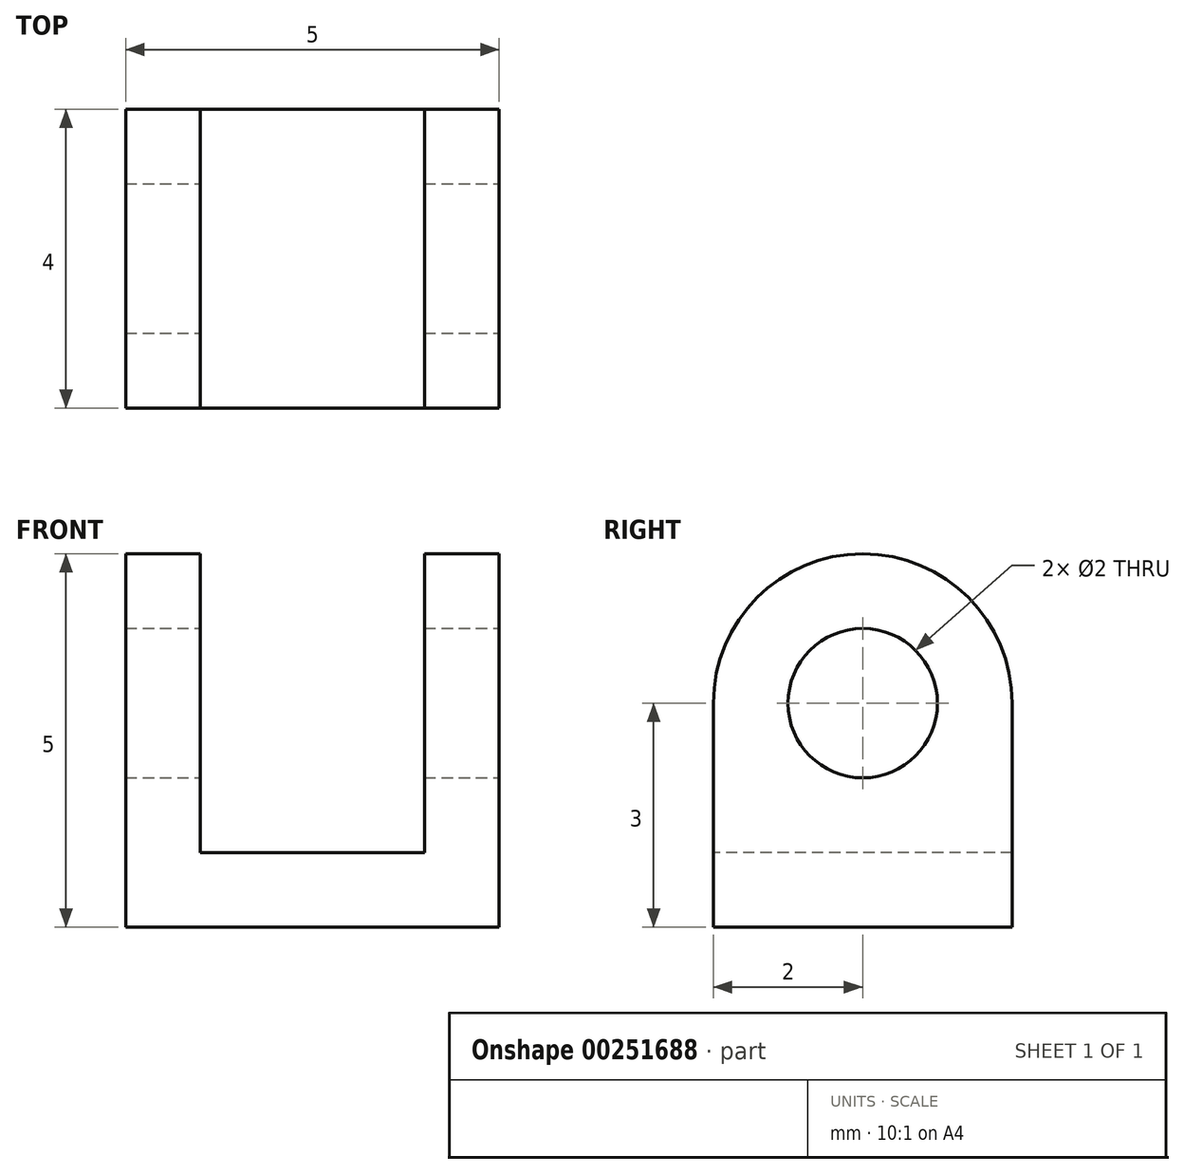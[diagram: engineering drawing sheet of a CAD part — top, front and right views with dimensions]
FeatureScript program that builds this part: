
annotation { "Feature Type Name" : "Feature", "Feature Type Description" : "" }
export const myFeature = defineFeature(function(context is Context, id is Id, definition is map)
    precondition{}
    {
        {
            var Q0;
            Q0=qCreatedBy(makeId("Top.planeOp"),FACE);
            var sketch = newSketch(context, id + "F0", { "sketchPlane" : qUnion([Q0])});
            skLineSegment(sketch, "E0.bottom", {"start": v(0, 0) * mm, "end": v(5, 0) * mm});
            skLineSegment(sketch, "E0.top", {"start": v(0, 4) * mm, "end": v(5, 4) * mm});
            skLineSegment(sketch, "E0.left", {"start": v(0, 0) * mm, "end": v(0, 4) * mm});
            skLineSegment(sketch, "E0.right", {"start": v(5, 0) * mm, "end": v(5, 4) * mm});
            skSolve(sketch);
        }
        {
            var Q0;
            Q0 = qSketchRegion(id + "F0", true);
            extrude(context, id + "F1", {"entities" : qUnion([Q0]), "depth" : 5 * mm});
        }
        {
            var Q0;
            Q0=makeQuery(id+"F1.opExtrude","CAP_EDGE",EDGE,{"disambiguationData":[OSD([sQuery(id+"F0.wireOp",EDGE,"E0.bottom")])],"isStart":false});
            var Q1;
            Q1=makeQuery(id+"F1.opExtrude","CAP_EDGE",EDGE,{"disambiguationData":[OSD([sQuery(id+"F0.wireOp",EDGE,"E0.top")])],"isStart":false});
            fillet(context, id + "F2", {"entities" : qUnion([Q0, Q1]), "radius" : 2 * mm, "tangentPropagation" : true, "allowEdgeOverflow" : false});
        }
        {
            var Q0;
            Q0=makeQuery(id+"F1.opExtrude","SWEPT_FACE",FACE,{"disambiguationData":[OSD([sQuery(id+"F0.wireOp",EDGE,"E0.right")])]});
            var sketch = newSketch(context, id + "F3", { "sketchPlane" : qUnion([Q0])});
            skLineSegment(sketch, "E1", {"start": v(2, 5) * mm, "end": v(2, 3) * mm, "construction": true});
            skPoint(sketch, "E1.endSnap0", {"position": v(2, 5) * mm});
            skCircle(sketch, "E2", {"center": v(2, 3) * mm, "radius": 1 * mm});
            skSolve(sketch);
        }
        {
            var Q0;
            Q0 = qSketchRegion(id + "F3", true);
            extrude(context, id + "F4", {"entities" : qUnion([Q0]), "operationType" : NewBodyOperationType.REMOVE, "oppositeDirection" : true, "depth" : 25 * mm});
        }
        {
            var Q0;
            {var subQ0=sQuery(id+"F0.wireOp",EDGE,"E0.top");Q0=makeQuery(id+"F2.opFillet","BLEND_VERTEX",VERTEX,{"blendedFrom":[makeQuery(id+"F1.opExtrude","CAP_EDGE",EDGE,{"disambiguationData":[OSD([subQ0])],"isStart":false}),makeQuery(id+"F1.opExtrude","SWEPT_FACE",FACE,{"disambiguationData":[OSD([subQ0])]}),makeQuery(id+"F1.opExtrude","SWEPT_FACE",FACE,{"disambiguationData":[OSD([sQuery(id+"F0.wireOp",EDGE,"E0.left")])]})],"blendedInto":[makeQuery(id+"F1.opExtrude","SWEPT_FACE",FACE,{"disambiguationData":[OSD([subQ0])]}),makeQuery(id+"F1.opExtrude","SWEPT_FACE",FACE,{"disambiguationData":[OSD([sQuery(id+"F0.wireOp",EDGE,"E0.left")])]})]});}
            var Q1;
            {var subQ0=sQuery(id+"F0.wireOp",EDGE,"E0.top");Q1=makeQuery(id+"F2.opFillet","BLEND_VERTEX",VERTEX,{"blendedFrom":[makeQuery(id+"F1.opExtrude","CAP_EDGE",EDGE,{"disambiguationData":[OSD([subQ0])],"isStart":false}),makeQuery(id+"F1.opExtrude","SWEPT_FACE",FACE,{"disambiguationData":[OSD([subQ0])]}),makeQuery(id+"F1.opExtrude","SWEPT_FACE",FACE,{"disambiguationData":[OSD([sQuery(id+"F0.wireOp",EDGE,"E0.right")])]})],"blendedInto":[makeQuery(id+"F1.opExtrude","SWEPT_FACE",FACE,{"disambiguationData":[OSD([subQ0])]}),makeQuery(id+"F1.opExtrude","SWEPT_FACE",FACE,{"disambiguationData":[OSD([sQuery(id+"F0.wireOp",EDGE,"E0.right")])]})]});}
            var Q2;
            {var subQ0=sQuery(id+"F0.wireOp",EDGE,"E0.bottom");Q2=makeQuery(id+"F2.opFillet","BLEND_VERTEX",VERTEX,{"blendedFrom":[makeQuery(id+"F1.opExtrude","CAP_EDGE",EDGE,{"disambiguationData":[OSD([subQ0])],"isStart":false}),makeQuery(id+"F1.opExtrude","SWEPT_FACE",FACE,{"disambiguationData":[OSD([subQ0])]}),makeQuery(id+"F1.opExtrude","SWEPT_FACE",FACE,{"disambiguationData":[OSD([sQuery(id+"F0.wireOp",EDGE,"E0.left")])]})],"blendedInto":[makeQuery(id+"F1.opExtrude","SWEPT_FACE",FACE,{"disambiguationData":[OSD([subQ0])]}),makeQuery(id+"F1.opExtrude","SWEPT_FACE",FACE,{"disambiguationData":[OSD([sQuery(id+"F0.wireOp",EDGE,"E0.left")])]})]});}
            cPlane(context, id + "F5", {"entities" : qUnion([Q0, Q1, Q2]), "cplaneType" : CPlaneType.THREE_POINT, "offset" : 25 * mm, "width" : 150 * mm, "height" : 150 * mm});
        }
        {
            var Q0;
            Q0=qCreatedBy(id+"F5.planeOp",FACE);
            cPlane(context, id + "F6", {"entities" : qUnion([Q0]), "cplaneType" : CPlaneType.OFFSET, "offset" : 2 * mm, "width" : 150 * mm, "height" : 150 * mm});
        }
        {
            var Q0;
            Q0=qCreatedBy(id+"F6.planeOp",FACE);
            var sketch = newSketch(context, id + "F7", { "sketchPlane" : qUnion([Q0])});
            skPoint(sketch, "E3.0", {"position": v(0, 4) * mm});
            skPoint(sketch, "E3.1", {"position": v(5, 4) * mm});
            skPoint(sketch, "E3.2", {"position": v(5, 0) * mm});
            skPoint(sketch, "E3.3", {"position": v(0, 0) * mm});
            skLineSegment(sketch, "E4", {"start": v(0, 4) * mm, "end": v(1, 4) * mm, "construction": true});
            skLineSegment(sketch, "E5", {"start": v(1, 4) * mm, "end": v(1, 0) * mm});
            skLineSegment(sketch, "E6", {"start": v(5, 4) * mm, "end": v(4, 4) * mm, "construction": true});
            skLineSegment(sketch, "E7", {"start": v(4, 4) * mm, "end": v(4, 0) * mm});
            skLineSegment(sketch, "E8", {"start": v(1, 0) * mm, "end": v(4, 0) * mm});
            skLineSegment(sketch, "E9", {"start": v(4, 4) * mm, "end": v(1, 4) * mm});
            skSolve(sketch);
        }
        {
            var Q0;
            Q0 = qSketchRegion(id + "F7", true);
            extrude(context, id + "F8", {"entities" : qUnion([Q0]), "operationType" : NewBodyOperationType.REMOVE, "oppositeDirection" : true, "depth" : 4 * mm});
        }
    });
